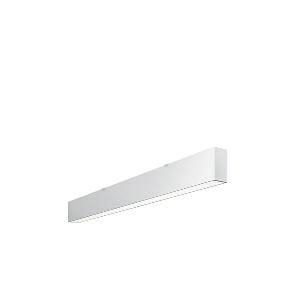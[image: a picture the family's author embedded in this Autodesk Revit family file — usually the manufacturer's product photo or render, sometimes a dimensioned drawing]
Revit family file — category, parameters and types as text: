
# Revit family: dotoo_line_-_dla_1000_830_d_end_00807939_42fc
name_source: partatom
category: Lighting Fixtures
units: mm (PartAtom-declared; Revit-internal decimal feet)

## family parameters
Cut with Voids When Loaded = No
Host = Face
Light Source = No
Part Type = Normal
Room Calculation Point = No
Round Connector Dimension = Use Diameter
Shared = No

## types (1)
- DOTOO.line - DLA 1000/830/D END (1 x LED, 1000 lm, 3000K)
    Apparent Load = 10 VA
    Approval mark = CE
    CIE Flux Codes = 67 91 98 100 100
    Color Rendering = 80-89
    Color Temperature = 3000K
    Control Gear = Electronic ballast
    Default Elevation = 1800 mm
    Description = DLA 1000/830/D|Surface-mounted luminaire.|light source: LED|work equipment: Adjustable electronic ballast, digital DALI|connected load: 220-240 V, 50/60 Hz|Power consumption: approx. 10 W|luminous flux: 1000 lm|luminous efficacy: 100 lm/W|light distribution: Direct|colour temperature: Warm white, ca. 3000 K|class of protection: I|technology: Continuously dimmable|mains lead: Connector|glare control: Prism aperture|special features: DALI Load 1x, TouchDIM - dimming via standard switch, Through-wired, up to 18 m on one mains connection, Flicker-free, Suitable as emergency lighting, Mechanical and electrical connection of the individual modules without tools|
    Frequency = 50 Hz
    Height = 110 mm
    Lamp = 1 x LED
    Lamp Light Flux = 1000 lm
    Lamp count = 1
    Length = 848 mm
    Luminous efficacy = 100 lm/W
    Manufacturer = Waldmann
    ModVariant = No
    Model = 00807939
    Mounting Place = Ceiling
    Mounting Type = Surface mounted
    Number of Poles = 1
    OnlyDefault = Yes
    Power Factor = 1
    Product Name = DOTOO.line - DLA 1000/830/D END
    Product group = Ceiling mounted luminaire
    ProductGroupID = 3
    Protection Class = Protection class I
    Protection Degree = IP 40
    RLX_Detail_Level = 1
    RLX_Emergency_Light_Flux = 0 lm
    RLX_Emergency_Type = 0
    RLX_Emergency_Type_DB = No
    RlxData = <blob elided: 15245 chars, md5=22205deb>
    Socket = socket
    Standby Power = 0 W
    System Light Flux = 1000 lm
    System Power = 10 W
    Type Comments = Product without accessories
    Type Image = 114350000-00807927.jpg
    URL = http://relux.com
    VarID = ---
    Voltage = 230 V
    Voltage Range = 220-240 V
    Weight = 0.00 kg
    Width = 60 mm  [stored 0.19685 ft]

note: [stored X ft] marks values corroborated as IEEE doubles in the binary element streams (Revit-internal decimal feet)

## geometry (parser evidence)
native form markers: Sweep x10
no freeform markers — native parametric forms only
